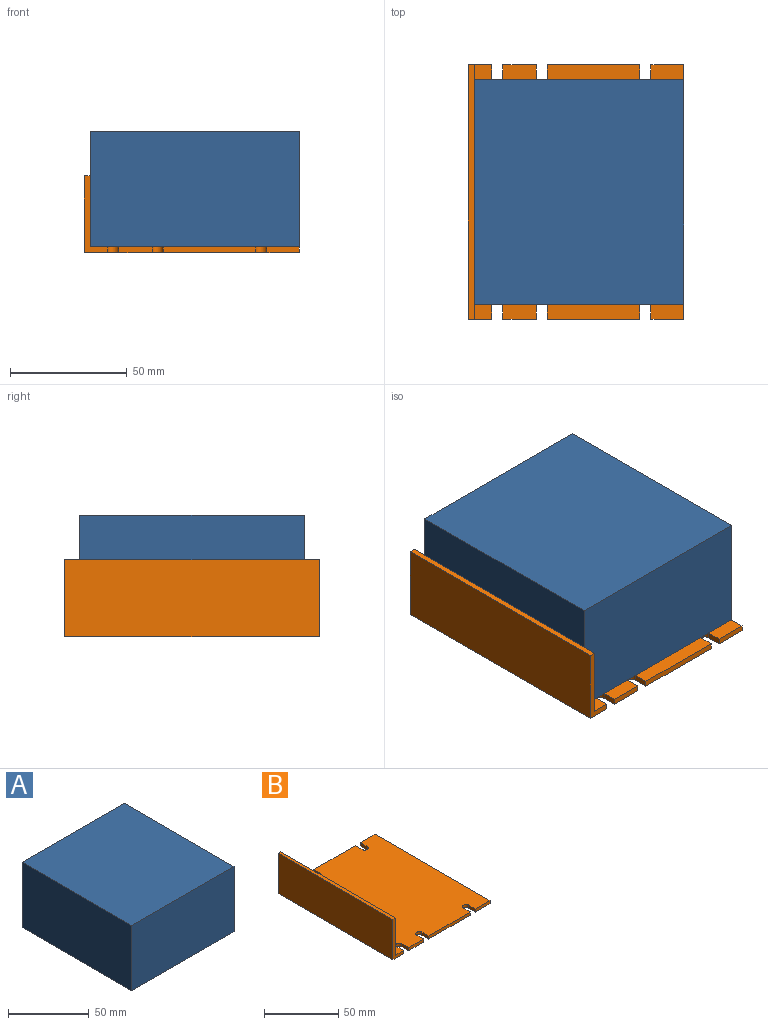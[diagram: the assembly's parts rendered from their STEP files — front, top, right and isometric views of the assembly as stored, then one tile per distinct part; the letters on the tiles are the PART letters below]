
ASSEMBLY  parts=2 mates=1
PART A: 6 faces, bbox 89.7x96.5x49.5 mm
  f0: plane 89.66x49.53mm, normal (0,-1,0), area 4441mm2, adj f1,f3,f4,f5
  f1: plane 96.52x49.53mm, normal (-1,0,0), area 4780.6mm2, adj f0,f2,f4,f5
  f2: plane 89.66x49.53mm, normal (0,1,0), area 4441mm2, adj f1,f3,f4,f5
  f3: plane 96.52x49.53mm, normal (1,0,0), area 4780.6mm2, adj f0,f2,f4,f5
  f4: plane 96.52x89.66mm, normal (0,0,1), area 8654.2mm2, adj f0,f1,f2,f3
  f5: plane 96.52x89.66mm, normal (0,0,-1), area 8654.2mm2, adj f0,f1,f2,f3
PART B: 32 faces, bbox 92.2x109.2x33 mm
  f0: plane 109.22x30.48mm, normal (1,0,0), area 3329mm2, adj f1,f2,f4,f30
  f1: plane 109.22x2.54mm, normal (0,0,1), area 277.4mm2, adj f0,f2,f3,f4
  f2: plane 33.02x10.03mm, normal (0,-1,0), area 102.9mm2, adj f0,f1,f3,f29,f30,f31
  f3: plane 109.22x33.02mm, normal (-1,0,0), area 3606.4mm2, adj f1,f2,f4,f31
  f4: plane 33.02x10.03mm, normal (0,1,0), area 102.9mm2, adj f0,f1,f3,f5,f30,f31
  f5: plane 6.35x2.54mm, normal (1,0,0), area 16.1mm2, adj f4,f6,f30,f31
  f6: cylinder r=2.41mm len=4.83mm, axis (0,0,1), area 19.3mm2, adj f5,f7,f30,f31
  f7: plane 6.35x2.54mm, normal (-1,0,0), area 16.1mm2, adj f6,f8,f30,f31
  f8: plane 14.22x2.54mm, normal (0,1,0), area 36.1mm2, adj f7,f9,f30,f31
  f9: plane 6.35x2.54mm, normal (1,0,0), area 16.1mm2, adj f8,f10,f30,f31
  f10: cylinder r=2.41mm len=4.83mm, axis (0,0,1), area 19.3mm2, adj f9,f11,f30,f31
  f11: plane 6.35x2.54mm, normal (-1,0,0), area 16.1mm2, adj f10,f12,f30,f31
  f12: plane 39.62x2.54mm, normal (0,1,0), area 100.6mm2, adj f11,f13,f30,f31
  f13: plane 6.35x2.54mm, normal (1,0,0), area 16.1mm2, adj f12,f14,f30,f31
  f14: cylinder r=2.41mm len=4.83mm, axis (0,0,1), area 19.3mm2, adj f13,f15,f30,f31
  f15: plane 6.35x2.54mm, normal (-1,0,0), area 16.1mm2, adj f14,f16,f30,f31
  f16: plane 13.84x2.54mm, normal (0,1,0), area 35.2mm2, adj f15,f17,f30,f31
  f17: plane 109.22x2.54mm, normal (1,0,0), area 277.4mm2, adj f16,f18,f30,f31
  f18: plane 13.84x2.54mm, normal (0,-1,0), area 35.2mm2, adj f17,f19,f30,f31
  f19: plane 6.35x2.54mm, normal (-1,0,0), area 16.1mm2, adj f18,f20,f30,f31
  f20: cylinder r=2.41mm len=4.83mm, axis (0,0,1), area 19.3mm2, adj f19,f21,f30,f31
  f21: plane 6.35x2.54mm, normal (1,0,0), area 16.1mm2, adj f20,f22,f30,f31
  f22: plane 39.62x2.54mm, normal (0,-1,0), area 100.6mm2, adj f21,f23,f30,f31
  f23: plane 6.35x2.54mm, normal (-1,0,0), area 16.1mm2, adj f22,f24,f30,f31
  f24: cylinder r=2.41mm len=4.83mm, axis (0,0,1), area 19.3mm2, adj f23,f25,f30,f31
  f25: plane 6.35x2.54mm, normal (1,0,0), area 16.1mm2, adj f24,f26,f30,f31
  f26: plane 14.22x2.54mm, normal (0,-1,0), area 36.1mm2, adj f25,f27,f30,f31
  f27: plane 6.35x2.54mm, normal (-1,0,0), area 16.1mm2, adj f26,f28,f30,f31
  f28: cylinder r=2.41mm len=4.83mm, axis (0,0,1), area 19.3mm2, adj f27,f29,f30,f31
  f29: plane 6.35x2.54mm, normal (1,0,0), area 16.1mm2, adj f2,f28,f30,f31
  f30: plane 109.22x89.66mm, normal (0,0,1), area 9554.1mm2, adj f0,f2,f4,f5,f6,f7,f8,f9
  f31: plane 109.22x92.2mm, normal (0,0,-1), area 9831.6mm2, adj f2,f3,f4,f5,f6,f7,f8,f9
PLACE A at identity
PLACE B t=(-0.19,0,0)mm
MATE fastened B.f30 <-> A.f5  axis (0,0,1) through (1.27,0,2.54)mm
